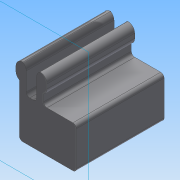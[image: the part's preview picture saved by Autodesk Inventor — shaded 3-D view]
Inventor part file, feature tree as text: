
AUTODESK INVENTOR PART (.ipt)
format: ipt  version: 2014 SP2 (Build 180246200, 246)  size: 126,464 bytes
history: native  units: mm
features: fillet x4, extrude x1, sketch x1
ambient origin geometry x8: Origin, YZ Plane, XZ Plane, XY Plane, X Axis, Y Axis, Z Axis, Center Point
bodies: Solid1 (feature_tree)
feature tree (6):
  extrude  "Extrusion1"  Depth=12.0mm
  fillet  "Fillet1"  Radius=2.0mm
  fillet  "Fillet2"  Radius=8.0mm
  fillet  "Fillet3"  Radius=3.0mm
  fillet  "Fillet4"  [1 undecoded]
  sketch  "Sketch1"  dims[d0=16.5mm d1=12.0mm d4=2.0mm d5=8.0mm d6=3.0mm d8=0.0mm d9=1.0mm d10=5.0mm d12=2.0mm d13=1.0mm d14=1.0mm d15=2.0mm]
note: 1 required parameter value undecoded (feature->parameter linkage not recoverable at this tier; creation-order binding heuristic only, values carry confidence <= 0.55)
